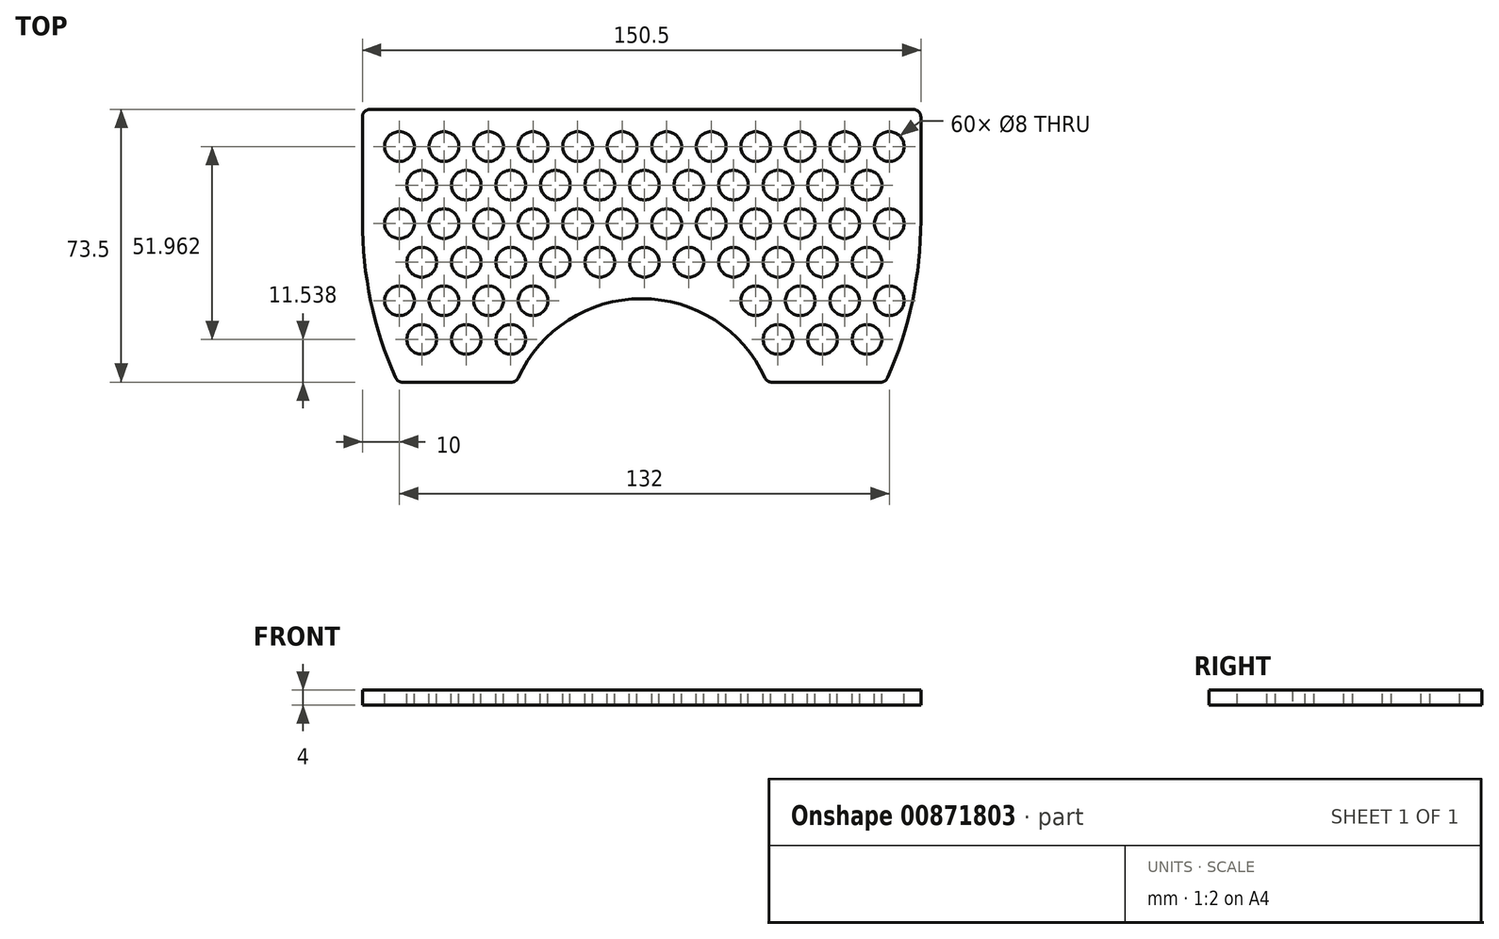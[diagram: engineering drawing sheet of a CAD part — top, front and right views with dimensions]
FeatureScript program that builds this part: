
annotation { "Feature Type Name" : "Feature", "Feature Type Description" : "" }
export const myFeature = defineFeature(function(context is Context, id is Id, definition is map)
    precondition{}
    {
        {
            var Q0;
            Q0=qCreatedBy(makeId("Top.planeOp"),FACE);
            var sketch = newSketch(context, id + "F0", { "sketchPlane" : qUnion([Q0])});
            skLineSegment(sketch, "E0", {"start": v(-75.25, 30) * mm, "end": v(75.25, 30) * mm});
            skLineSegment(sketch, "E1", {"start": v(-65.75, -43.5) * mm, "end": v(-33.75, -43.5) * mm});
            skLineSegment(sketch, "E2", {"start": v(33.75, -43.5) * mm, "end": v(65.75, -43.5) * mm});
            skLineSegment(sketch, "E3", {"start": v(0, 70.92) * mm, "end": v(0, 0) * mm, "construction": true});
            skArc(sketch, "E4", {"start": v(33.75, -43.5) * mm, "mid": v(0, -21) * mm, "end": v(-33.75, -43.5) * mm});
            skLineSegment(sketch, "E5", {"start": v(-75.25, 30) * mm, "end": v(-75.25, 0) * mm});
            skLineSegment(sketch, "E6", {"start": v(75.25, 30) * mm, "end": v(75.25, 0) * mm});
            skArc(sketch, "E7", {"start": v(-75.25, 0) * mm, "mid": v(-72.85, -22.26) * mm, "end": v(-65.75, -43.5) * mm});
            skArc(sketch, "E8", {"start": v(65.75, -43.5) * mm, "mid": v(72.85, -22.26) * mm, "end": v(75.25, 0) * mm});
            skSolve(sketch);
        }
        {
            var Q0;
            Q0 = qSketchRegion(id + "F0", true);
            extrude(context, id + "F1", {"entities" : qUnion([Q0]), "depth" : 4 * mm, "offsetDistance" : 25 * mm});
        }
        {
            var Q0;
            Q0=makeQuery(id+"F1.opExtrude","CAP_FACE",FACE,{"disambiguationData":[OSD([sQuery(id+"F0.wireOp",EDGE,"E0"),sQuery(id+"F0.wireOp",EDGE,"E1"),sQuery(id+"F0.wireOp",EDGE,"E2"),sQuery(id+"F0.wireOp",EDGE,"E4"),sQuery(id+"F0.wireOp",EDGE,"E5"),sQuery(id+"F0.wireOp",EDGE,"E6"),sQuery(id+"F0.wireOp",EDGE,"E7"),sQuery(id+"F0.wireOp",EDGE,"E8")])],"isStart":false});
            var sketch = newSketch(context, id + "F2", { "sketchPlane" : qUnion([Q0])});
            skCircle(sketch, "E9", {"center": v(-89.25, 20) * mm, "radius": 4 * mm, "construction": true});
            skCircle(sketch, "E10.0.1.0", {"center": v(-83.25, 9.6) * mm, "radius": 4 * mm, "construction": true});
            skCircle(sketch, "E10.1.0.0", {"center": v(-77.25, 20) * mm, "radius": 4 * mm, "construction": true});
            skCircle(sketch, "E10.1.1.0", {"center": v(-71.25, 9.6) * mm, "radius": 4 * mm, "construction": true});
            skCircle(sketch, "E10.2.0.0", {"center": v(-65.25, 20) * mm, "radius": 4 * mm});
            skCircle(sketch, "E10.2.1.0", {"center": v(-59.25, 9.6) * mm, "radius": 4 * mm});
            skLineSegment(sketch, "E10.direction1", {"start": v(-89.25, 20) * mm, "end": v(-77.25, 20) * mm, "construction": true});
            skLineSegment(sketch, "E10.direction2", {"start": v(-89.25, 20) * mm, "end": v(-83.25, 9.6) * mm, "construction": true});
            skCircle(sketch, "E11.0.3.0", {"center": v(-53.25, 20) * mm, "radius": 4 * mm});
            skCircle(sketch, "E11.0.3.1", {"center": v(-47.25, 9.6) * mm, "radius": 4 * mm});
            skCircle(sketch, "E11.0.4.0", {"center": v(-41.25, 20) * mm, "radius": 4 * mm});
            skCircle(sketch, "E11.0.4.1", {"center": v(-35.25, 9.6) * mm, "radius": 4 * mm});
            skCircle(sketch, "E11.0.5.0", {"center": v(-29.25, 20) * mm, "radius": 4 * mm});
            skCircle(sketch, "E11.0.5.1", {"center": v(-23.25, 9.6) * mm, "radius": 4 * mm});
            skCircle(sketch, "E11.0.6.0", {"center": v(-17.25, 20) * mm, "radius": 4 * mm});
            skCircle(sketch, "E11.0.6.1", {"center": v(-11.25, 9.6) * mm, "radius": 4 * mm});
            skCircle(sketch, "E11.0.7.0", {"center": v(-5.25, 20) * mm, "radius": 4 * mm});
            skCircle(sketch, "E11.0.7.1", {"center": v(0.75, 9.6) * mm, "radius": 4 * mm});
            skCircle(sketch, "E11.0.8.0", {"center": v(6.75, 20) * mm, "radius": 4 * mm});
            skCircle(sketch, "E11.0.8.1", {"center": v(12.75, 9.6) * mm, "radius": 4 * mm});
            skCircle(sketch, "E11.0.9.0", {"center": v(18.75, 20) * mm, "radius": 4 * mm});
            skCircle(sketch, "E11.0.9.1", {"center": v(24.75, 9.6) * mm, "radius": 4 * mm});
            skCircle(sketch, "E11.0.10.0", {"center": v(30.75, 20) * mm, "radius": 4 * mm});
            skCircle(sketch, "E11.0.10.1", {"center": v(36.75, 9.6) * mm, "radius": 4 * mm});
            skCircle(sketch, "E11.0.11.0", {"center": v(42.75, 20) * mm, "radius": 4 * mm});
            skCircle(sketch, "E11.0.11.1", {"center": v(48.75, 9.6) * mm, "radius": 4 * mm});
            skCircle(sketch, "E11.0.12.0", {"center": v(54.75, 20) * mm, "radius": 4 * mm});
            skCircle(sketch, "E11.0.12.1", {"center": v(60.75, 9.6) * mm, "radius": 4 * mm});
            skCircle(sketch, "E11.0.13.0", {"center": v(66.75, 20) * mm, "radius": 4 * mm});
            skCircle(sketch, "E11.0.13.1", {"center": v(72.75, 9.6) * mm, "radius": 4 * mm, "construction": true});
            skCircle(sketch, "E12.0.0.2", {"center": v(-77.25, -0.78) * mm, "radius": 4 * mm, "construction": true});
            skCircle(sketch, "E12.0.0.3", {"center": v(-71.25, -11.18) * mm, "radius": 4 * mm, "construction": true});
            skCircle(sketch, "E12.0.0.4", {"center": v(-65.25, -21.57) * mm, "radius": 4 * mm});
            skCircle(sketch, "E12.0.0.5", {"center": v(-59.25, -31.96) * mm, "radius": 4 * mm});
            skCircle(sketch, "E12.0.1.2", {"center": v(-65.25, -0.78) * mm, "radius": 4 * mm});
            skCircle(sketch, "E12.0.1.3", {"center": v(-59.25, -11.18) * mm, "radius": 4 * mm});
            skCircle(sketch, "E12.0.1.4", {"center": v(-53.25, -21.57) * mm, "radius": 4 * mm});
            skCircle(sketch, "E12.0.1.5", {"center": v(-47.25, -31.96) * mm, "radius": 4 * mm});
            skCircle(sketch, "E12.0.2.2", {"center": v(-53.25, -0.78) * mm, "radius": 4 * mm});
            skCircle(sketch, "E12.0.2.3", {"center": v(-47.25, -11.18) * mm, "radius": 4 * mm});
            skCircle(sketch, "E12.0.2.4", {"center": v(-41.25, -21.57) * mm, "radius": 4 * mm});
            skCircle(sketch, "E12.0.2.5", {"center": v(-35.25, -31.96) * mm, "radius": 4 * mm});
            skCircle(sketch, "E12.0.3.2", {"center": v(-41.25, -0.78) * mm, "radius": 4 * mm});
            skCircle(sketch, "E12.0.3.3", {"center": v(-35.25, -11.18) * mm, "radius": 4 * mm});
            skCircle(sketch, "E12.0.3.4", {"center": v(-29.25, -21.57) * mm, "radius": 4 * mm});
            skCircle(sketch, "E12.0.3.5", {"center": v(-23.25, -31.96) * mm, "radius": 4 * mm, "construction": true});
            skCircle(sketch, "E12.0.4.2", {"center": v(-29.25, -0.78) * mm, "radius": 4 * mm});
            skCircle(sketch, "E12.0.4.3", {"center": v(-23.25, -11.18) * mm, "radius": 4 * mm});
            skCircle(sketch, "E12.0.4.4", {"center": v(-17.25, -21.57) * mm, "radius": 4 * mm, "construction": true});
            skCircle(sketch, "E12.0.4.5", {"center": v(-11.25, -31.96) * mm, "radius": 4 * mm, "construction": true});
            skCircle(sketch, "E12.0.5.2", {"center": v(-17.25, -0.78) * mm, "radius": 4 * mm});
            skCircle(sketch, "E12.0.5.3", {"center": v(-11.25, -11.18) * mm, "radius": 4 * mm});
            skCircle(sketch, "E12.0.5.4", {"center": v(-5.25, -21.57) * mm, "radius": 4 * mm, "construction": true});
            skCircle(sketch, "E12.0.5.5", {"center": v(0.75, -31.96) * mm, "radius": 4 * mm, "construction": true});
            skCircle(sketch, "E12.0.6.2", {"center": v(-5.25, -0.78) * mm, "radius": 4 * mm});
            skCircle(sketch, "E12.0.6.3", {"center": v(0.75, -11.18) * mm, "radius": 4 * mm});
            skCircle(sketch, "E12.0.6.4", {"center": v(6.75, -21.57) * mm, "radius": 4 * mm, "construction": true});
            skCircle(sketch, "E12.0.6.5", {"center": v(12.75, -31.96) * mm, "radius": 4 * mm, "construction": true});
            skCircle(sketch, "E12.0.7.2", {"center": v(6.75, -0.78) * mm, "radius": 4 * mm});
            skCircle(sketch, "E12.0.7.3", {"center": v(12.75, -11.18) * mm, "radius": 4 * mm});
            skCircle(sketch, "E12.0.7.4", {"center": v(18.75, -21.57) * mm, "radius": 4 * mm, "construction": true});
            skCircle(sketch, "E12.0.7.5", {"center": v(24.75, -31.96) * mm, "radius": 4 * mm, "construction": true});
            skCircle(sketch, "E12.0.8.2", {"center": v(18.75, -0.78) * mm, "radius": 4 * mm});
            skCircle(sketch, "E12.0.8.3", {"center": v(24.75, -11.18) * mm, "radius": 4 * mm});
            skCircle(sketch, "E12.0.8.4", {"center": v(30.75, -21.57) * mm, "radius": 4 * mm});
            skCircle(sketch, "E12.0.8.5", {"center": v(36.75, -31.96) * mm, "radius": 4 * mm});
            skCircle(sketch, "E12.0.9.2", {"center": v(30.75, -0.78) * mm, "radius": 4 * mm});
            skCircle(sketch, "E12.0.9.3", {"center": v(36.75, -11.18) * mm, "radius": 4 * mm});
            skCircle(sketch, "E12.0.9.4", {"center": v(42.75, -21.57) * mm, "radius": 4 * mm});
            skCircle(sketch, "E12.0.9.5", {"center": v(48.75, -31.96) * mm, "radius": 4 * mm});
            skCircle(sketch, "E12.0.10.2", {"center": v(42.75, -0.78) * mm, "radius": 4 * mm});
            skCircle(sketch, "E12.0.10.3", {"center": v(48.75, -11.18) * mm, "radius": 4 * mm});
            skCircle(sketch, "E12.0.10.4", {"center": v(54.75, -21.57) * mm, "radius": 4 * mm});
            skCircle(sketch, "E12.0.10.5", {"center": v(60.75, -31.96) * mm, "radius": 4 * mm});
            skCircle(sketch, "E12.0.11.2", {"center": v(54.75, -0.78) * mm, "radius": 4 * mm});
            skCircle(sketch, "E12.0.11.3", {"center": v(60.75, -11.18) * mm, "radius": 4 * mm});
            skCircle(sketch, "E12.0.11.4", {"center": v(66.75, -21.57) * mm, "radius": 4 * mm});
            skCircle(sketch, "E12.0.11.5", {"center": v(72.75, -31.96) * mm, "radius": 4 * mm, "construction": true});
            skCircle(sketch, "E12.0.12.2", {"center": v(66.75, -0.78) * mm, "radius": 4 * mm});
            skCircle(sketch, "E12.0.12.3", {"center": v(72.75, -11.18) * mm, "radius": 4 * mm, "construction": true});
            skCircle(sketch, "E12.0.12.4", {"center": v(78.75, -21.57) * mm, "radius": 4 * mm, "construction": true});
            skCircle(sketch, "E12.0.12.5", {"center": v(84.75, -31.96) * mm, "radius": 4 * mm, "construction": true});
            skCircle(sketch, "E12.0.13.2", {"center": v(78.75, -0.78) * mm, "radius": 4 * mm, "construction": true});
            skCircle(sketch, "E12.0.13.3", {"center": v(84.75, -11.18) * mm, "radius": 4 * mm, "construction": true});
            skCircle(sketch, "E12.0.13.4", {"center": v(90.75, -21.57) * mm, "radius": 4 * mm, "construction": true});
            skCircle(sketch, "E12.0.13.5", {"center": v(96.75, -31.96) * mm, "radius": 4 * mm, "construction": true});
            skSolve(sketch);
        }
        {
            var Q0;
            Q0 = qSketchRegion(id + "F2", true);
            extrude(context, id + "F3", {"entities" : qUnion([Q0]), "operationType" : NewBodyOperationType.REMOVE, "endBound" : BoundingType.THROUGH_ALL, "oppositeDirection" : true, "depth" : 25 * mm, "offsetDistance" : 25 * mm});
        }
        {
            var Q0;
            Q0=makeQuery(id+"F1.opExtrude","SWEPT_EDGE",EDGE,{"disambiguationData":[OSD([sQuery(id+"F0.wireOp",EDGE,"E0"),sQuery(id+"F0.wireOp",EDGE,"E5")])]});
            var Q1;
            Q1=makeQuery(id+"F1.opExtrude","SWEPT_EDGE",EDGE,{"disambiguationData":[OSD([sQuery(id+"F0.wireOp",EDGE,"E1"),sQuery(id+"F0.wireOp",EDGE,"E7")])]});
            var Q2;
            Q2=makeQuery(id+"F1.opExtrude","SWEPT_EDGE",EDGE,{"disambiguationData":[OSD([sQuery(id+"F0.wireOp",EDGE,"E1"),sQuery(id+"F0.wireOp",EDGE,"E4")])]});
            var Q3;
            Q3=makeQuery(id+"F1.opExtrude","SWEPT_EDGE",EDGE,{"disambiguationData":[OSD([sQuery(id+"F0.wireOp",EDGE,"E2"),sQuery(id+"F0.wireOp",EDGE,"E4")])]});
            var Q4;
            Q4=makeQuery(id+"F1.opExtrude","SWEPT_EDGE",EDGE,{"disambiguationData":[OSD([sQuery(id+"F0.wireOp",EDGE,"E2"),sQuery(id+"F0.wireOp",EDGE,"E8")])]});
            var Q5;
            Q5=makeQuery(id+"F1.opExtrude","SWEPT_EDGE",EDGE,{"disambiguationData":[OSD([sQuery(id+"F0.wireOp",EDGE,"E0"),sQuery(id+"F0.wireOp",EDGE,"E6")])]});
            fillet(context, id + "F4", {"entities" : qUnion([Q0, Q1, Q2, Q3, Q4, Q5]), "tangentPropagation" : true, "radius" : 2 * mm, "defaultsChanged" : false, "vertexSettings" : [], "allowEdgeOverflow" : false});
        }
    });
